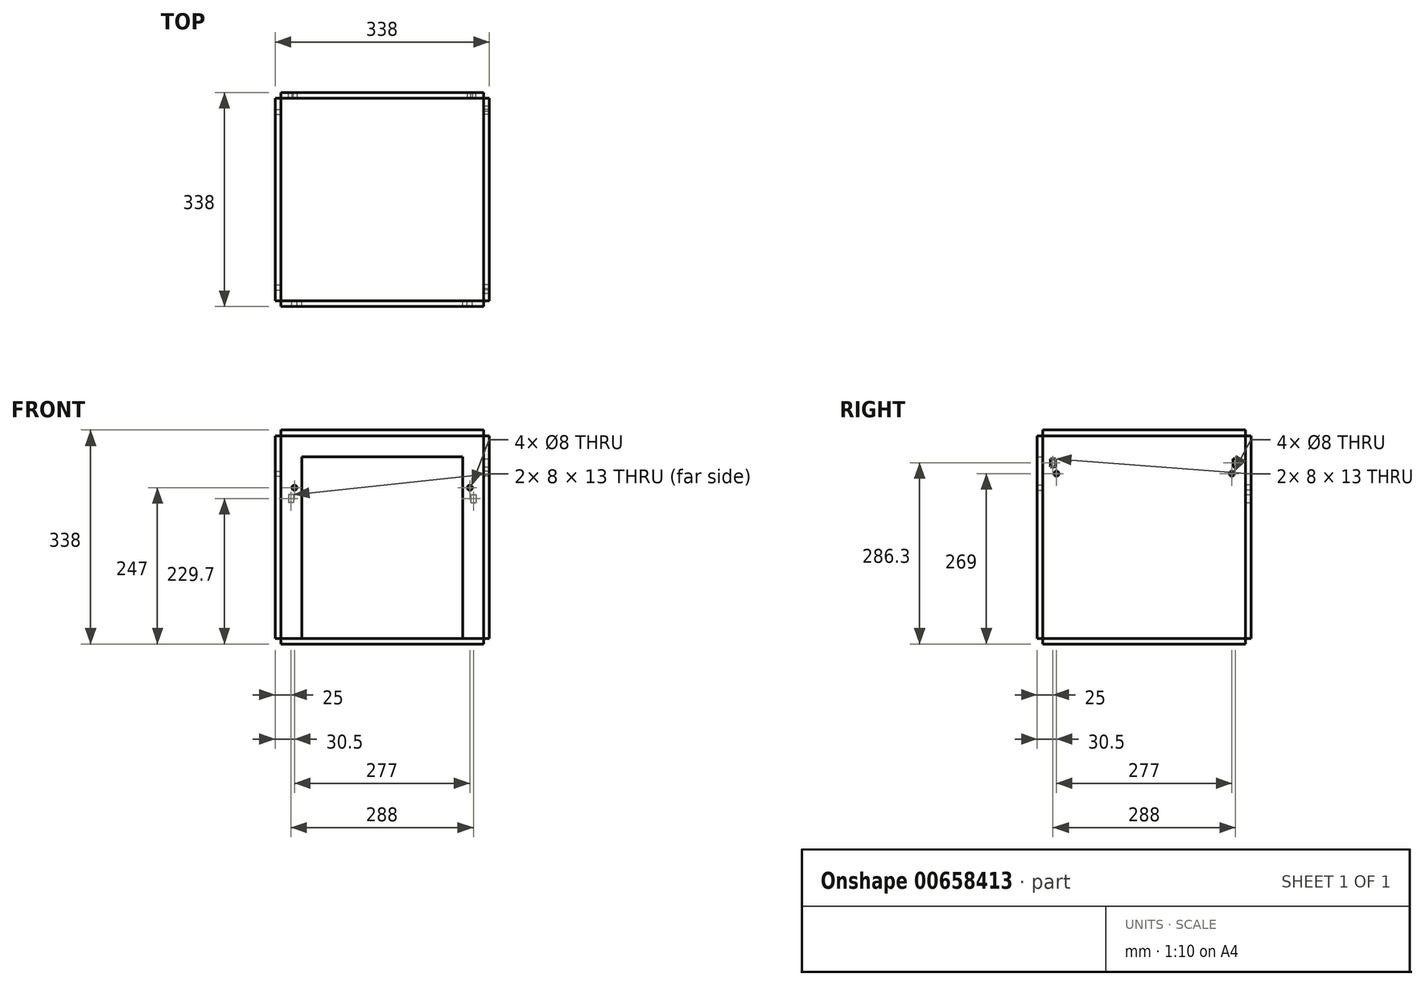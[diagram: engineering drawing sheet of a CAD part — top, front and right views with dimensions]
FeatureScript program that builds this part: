
annotation { "Feature Type Name" : "Feature", "Feature Type Description" : "" }
export const myFeature = defineFeature(function(context is Context, id is Id, definition is map)
    precondition{}
    {
        {
            assignVariable(context, id + "F0", {"name" : "wood", "anyValue" : 9});
        }
        {
            var Q0;
            Q0=qCreatedBy(makeId("Top.planeOp"),FACE);
            var sketch = newSketch(context, id + "F1", { "sketchPlane" : qUnion([Q0])});
            skLineSegment(sketch, "E0.bottom", {"start": v(160, 160) * mm, "end": v(-160, 160) * mm});
            skLineSegment(sketch, "E0.top", {"start": v(160, -160) * mm, "end": v(-160, -160) * mm});
            skLineSegment(sketch, "E0.left", {"start": v(160, 160) * mm, "end": v(160, -160) * mm});
            skLineSegment(sketch, "E0.right", {"start": v(-160, 160) * mm, "end": v(-160, -160) * mm});
            skPoint(sketch, "E0.middle", {"position": v(0, 0) * mm});
            skSolve(sketch);
        }
        {
            var Q0;
            Q0=makeQuery(id+"F1.imprint","IMPRINT",FACE,{"disambiguationData":[TD([[makeQuery(id+"F1.imprint","IMPRINT",EDGE,{"derivedFrom":sQuery(id+"F1.wireOp",EDGE,"E0.bottom")}),1.0]])]});
            extrude(context, id + "F2", {"entities" : qUnion([Q0]), "oppositeDirection" : true, "depth" : (getVariable(context, 'wood')) * mm, "offsetDistance" : 25 * mm});
        }
        {
            var Q0;
            Q0=makeQuery(id+"F2.opExtrude","SWEPT_FACE",FACE,{"disambiguationData":[OSD([sQuery(id+"F1.wireOp",EDGE,"E0.right")])]});
            var sketch = newSketch(context, id + "F3", { "sketchPlane" : qUnion([Q0])});
            skLineSegment(sketch, "E1.bottom", {"start": v(-160, 0) * mm, "end": v(160, 0) * mm});
            skLineSegment(sketch, "E1.top", {"start": v(-160, 320) * mm, "end": v(160, 320) * mm});
            skLineSegment(sketch, "E1.left", {"start": v(-160, 0) * mm, "end": v(-160, 320) * mm});
            skLineSegment(sketch, "E1.right", {"start": v(160, 0) * mm, "end": v(160, 320) * mm});
            skCircle(sketch, "E2", {"center": v(-138.5, 260) * mm, "radius": 4 * mm});
            skCircle(sketch, "E3.MirrorC", {"center": v(138.5, 260) * mm, "radius": 4 * mm});
            skSolve(sketch);
        }
        {
            var Q0;
            Q0=makeQuery(id+"F3.imprint","IMPRINT",FACE,{"disambiguationData":[TD([[makeQuery(id+"F3.imprint","IMPRINT",EDGE,{"derivedFrom":sQuery(id+"F3.wireOp",EDGE,"E1.bottom")}),1.0]])]});
            extrude(context, id + "F4", {"entities" : qUnion([Q0]), "depth" : (getVariable(context, 'wood')) * mm, "offsetDistance" : 25 * mm});
        }
        {
            var Q0;
            Q0=makeQuery(id+"F4.opExtrude","SWEPT_BODY",BODY,{"disambiguationData":[OSD([sQuery(id+"F3.wireOp",EDGE,"E1.bottom"),sQuery(id+"F3.wireOp",EDGE,"E1.top"),sQuery(id+"F3.wireOp",EDGE,"E1.left"),sQuery(id+"F3.wireOp",EDGE,"E1.right")])]});
            var Q1;
            Q1=qCreatedBy(makeId("Right.planeOp"),FACE);
            mirror(context, id + "F5", {"entities" : qUnion([Q0]), "mirrorPlane" : qUnion([Q1])});
        }
        {
            var Q0;
            Q0=makeQuery(id+"F2.opExtrude","SWEPT_FACE",FACE,{"disambiguationData":[OSD([sQuery(id+"F1.wireOp",EDGE,"E0.top")])]});
            var sketch = newSketch(context, id + "F6", { "sketchPlane" : qUnion([Q0])});
            skLineSegment(sketch, "E4.bottom", {"start": v(-160, 0) * mm, "end": v(160, 0) * mm});
            skLineSegment(sketch, "E4.top", {"start": v(-160, 320) * mm, "end": v(160, 320) * mm});
            skLineSegment(sketch, "E4.left", {"start": v(-160, 0) * mm, "end": v(-160, 320) * mm});
            skLineSegment(sketch, "E4.right", {"start": v(160, 0) * mm, "end": v(160, 320) * mm});
            skLineSegment(sketch, "E5", {"start": v(-127, 0) * mm, "end": v(-127, 287) * mm});
            skLineSegment(sketch, "E6.MirrorCS", {"start": v(127, 0) * mm, "end": v(127, 287) * mm});
            skLineSegment(sketch, "E7", {"start": v(-127, 287) * mm, "end": v(127, 287) * mm});
            skCircle(sketch, "E8", {"center": v(-138.5, 238) * mm, "radius": 4 * mm});
            skCircle(sketch, "E9.MirrorC", {"center": v(138.5, 238) * mm, "radius": 4 * mm});
            skSolve(sketch);
        }
        {
            var Q0;
            Q0=makeQuery(id+"F2.opExtrude","SWEPT_FACE",FACE,{"disambiguationData":[OSD([sQuery(id+"F1.wireOp",EDGE,"E0.bottom")])]});
            var sketch = newSketch(context, id + "F7", { "sketchPlane" : qUnion([Q0])});
            skLineSegment(sketch, "E10.bottom", {"start": v(-160, 0) * mm, "end": v(160, 0) * mm});
            skLineSegment(sketch, "E10.top", {"start": v(-160, 320) * mm, "end": v(160, 320) * mm});
            skLineSegment(sketch, "E10.left", {"start": v(-160, 0) * mm, "end": v(-160, 320) * mm});
            skLineSegment(sketch, "E10.right", {"start": v(160, 0) * mm, "end": v(160, 320) * mm});
            skCircle(sketch, "E11", {"center": v(-138.5, 238) * mm, "radius": 4 * mm});
            skCircle(sketch, "E12", {"center": v(138.5, 238) * mm, "radius": 4 * mm});
            skSolve(sketch);
        }
        {
            var Q0;
            Q0=makeQuery(id+"F7.imprint","IMPRINT",FACE,{"disambiguationData":[TD([[makeQuery(id+"F7.imprint","IMPRINT",EDGE,{"derivedFrom":sQuery(id+"F7.wireOp",EDGE,"E10.bottom")}),1.0]])]});
            extrude(context, id + "F8", {"entities" : qUnion([Q0]), "depth" : (getVariable(context, 'wood')) * mm, "offsetDistance" : 25 * mm});
        }
        {
            var Q0;
            Q0=makeQuery(id+"F6.imprint","IMPRINT",FACE,{"disambiguationData":[TD([[makeQuery(id+"F6.imprint","IMPRINT",EDGE,{"derivedFrom":sQuery(id+"F6.wireOp",EDGE,"E4.bottom")}),-1.0]])]});
            extrude(context, id + "F9", {"entities" : qUnion([Q0]), "depth" : (getVariable(context, 'wood')) * mm, "offsetDistance" : 25 * mm});
        }
        {
            var Q0;
            Q0=makeQuery(id+"F8.opExtrude","SWEPT_FACE",FACE,{"disambiguationData":[OSD([sQuery(id+"F7.wireOp",EDGE,"E10.top")])]});
            var sketch = newSketch(context, id + "F10", { "sketchPlane" : qUnion([Q0])});
            skLineSegment(sketch, "E13.bottom", {"start": v(-160, 160) * mm, "end": v(160, 160) * mm});
            skLineSegment(sketch, "E13.top", {"start": v(-160, -160) * mm, "end": v(160, -160) * mm});
            skLineSegment(sketch, "E13.left", {"start": v(-160, 160) * mm, "end": v(-160, -160) * mm});
            skLineSegment(sketch, "E13.right", {"start": v(160, 160) * mm, "end": v(160, -160) * mm});
            skSolve(sketch);
        }
        {
            var Q0;
            Q0=makeQuery(id+"F10.imprint","IMPRINT",FACE,{"disambiguationData":[TD([[makeQuery(id+"F10.imprint","IMPRINT",EDGE,{"derivedFrom":sQuery(id+"F10.wireOp",EDGE,"E13.bottom")}),1.0]])]});
            extrude(context, id + "F11", {"entities" : qUnion([Q0]), "depth" : (getVariable(context, 'wood')) * mm, "offsetDistance" : 25 * mm});
        }
        {
            var Q0;
            Q0=makeQuery(id+"F5.opPattern","COPY",FACE,{"derivedFrom":makeQuery(id+"F4.opExtrude","CAP_FACE",FACE,{"disambiguationData":[OSD([sQuery(id+"F3.wireOp",EDGE,"E1.bottom"),sQuery(id+"F3.wireOp",EDGE,"E1.top"),sQuery(id+"F3.wireOp",EDGE,"E1.left"),sQuery(id+"F3.wireOp",EDGE,"E1.right"),sQuery(id+"F3.wireOp",EDGE,"E2"),sQuery(id+"F3.wireOp",EDGE,"E3.MirrorC")])],"isStart":false}),"instanceName":"1"});
            var sketch = newSketch(context, id + "F12", { "sketchPlane" : qUnion([Q0])});
            skLineSegment(sketch, "E14.bottom", {"start": v(-140, 283.8) * mm, "end": v(-148, 283.8) * mm});
            skLineSegment(sketch, "E14.top", {"start": v(-140, 270.8) * mm, "end": v(-148, 270.8) * mm});
            skLineSegment(sketch, "E14.left", {"start": v(-140, 283.8) * mm, "end": v(-140, 270.8) * mm});
            skLineSegment(sketch, "E14.right", {"start": v(-148, 283.8) * mm, "end": v(-148, 270.8) * mm});
            skPoint(sketch, "E14.middle", {"position": v(-144, 277.3) * mm});
            skPoint(sketch, "E15", {"position": v(-138.5, 260) * mm});
            skLineSegment(sketch, "E16.MirrorCS", {"start": v(148, 283.8) * mm, "end": v(148, 270.8) * mm});
            skPoint(sketch, "E17.MirrorP", {"position": v(144, 277.3) * mm});
            skLineSegment(sketch, "E18.MirrorCS", {"start": v(140, 283.8) * mm, "end": v(148, 283.8) * mm});
            skLineSegment(sketch, "E19.MirrorCS", {"start": v(140, 283.8) * mm, "end": v(140, 270.8) * mm});
            skLineSegment(sketch, "E20.MirrorCS", {"start": v(140, 270.8) * mm, "end": v(148, 270.8) * mm});
            skSolve(sketch);
        }
        {
            var Q0;
            Q0=makeQuery(id+"F12.imprint","IMPRINT",FACE,{"disambiguationData":[TD([[makeQuery(id+"F12.imprint","IMPRINT",EDGE,{"derivedFrom":sQuery(id+"F12.wireOp",EDGE,"E14.bottom")}),1.0]])]});
            var Q1;
            Q1=makeQuery(id+"F12.imprint","IMPRINT",FACE,{"disambiguationData":[TD([[makeQuery(id+"F12.imprint","IMPRINT",EDGE,{"derivedFrom":sQuery(id+"F12.wireOp",EDGE,"E16.MirrorCS")}),-1.0]])]});
            extrude(context, id + "F13", {"entities" : qUnion([Q0, Q1]), "operationType" : NewBodyOperationType.REMOVE, "endBound" : BoundingType.UP_TO_NEXT, "oppositeDirection" : true, "depth" : 25 * mm, "offsetDistance" : 25 * mm});
        }
        {
            var Q0;
            Q0=makeQuery(id+"F8.opExtrude","CAP_FACE",FACE,{"disambiguationData":[OSD([sQuery(id+"F7.wireOp",EDGE,"E10.bottom"),sQuery(id+"F7.wireOp",EDGE,"E10.top"),sQuery(id+"F7.wireOp",EDGE,"E10.left"),sQuery(id+"F7.wireOp",EDGE,"E10.right"),sQuery(id+"F7.wireOp",EDGE,"E11"),sQuery(id+"F7.wireOp",EDGE,"E12")])],"isStart":false});
            var sketch = newSketch(context, id + "F14", { "sketchPlane" : qUnion([Q0])});
            skLineSegment(sketch, "E21.bottom", {"start": v(-140, 227.2) * mm, "end": v(-148, 227.2) * mm});
            skLineSegment(sketch, "E21.top", {"start": v(-140, 214.2) * mm, "end": v(-148, 214.2) * mm});
            skLineSegment(sketch, "E21.left", {"start": v(-140, 227.2) * mm, "end": v(-140, 214.2) * mm});
            skLineSegment(sketch, "E21.right", {"start": v(-148, 227.2) * mm, "end": v(-148, 214.2) * mm});
            skPoint(sketch, "E21.middle", {"position": v(-144, 220.7) * mm});
            skPoint(sketch, "E22", {"position": v(-138.5, 238) * mm});
            skPoint(sketch, "E23.MirrorP", {"position": v(144, 220.7) * mm});
            skLineSegment(sketch, "E24.MirrorCS", {"start": v(140, 227.2) * mm, "end": v(148, 227.2) * mm});
            skLineSegment(sketch, "E25.MirrorCS", {"start": v(140, 214.2) * mm, "end": v(148, 214.2) * mm});
            skLineSegment(sketch, "E26.MirrorCS", {"start": v(140, 227.2) * mm, "end": v(140, 214.2) * mm});
            skLineSegment(sketch, "E27.MirrorCS", {"start": v(148, 227.2) * mm, "end": v(148, 214.2) * mm});
            skSolve(sketch);
        }
        {
            var Q0;
            Q0=makeQuery(id+"F14.imprint","IMPRINT",FACE,{"disambiguationData":[TD([[makeQuery(id+"F14.imprint","IMPRINT",EDGE,{"derivedFrom":sQuery(id+"F14.wireOp",EDGE,"E21.bottom")}),1.0]])]});
            var Q1;
            Q1=makeQuery(id+"F14.imprint","IMPRINT",FACE,{"disambiguationData":[TD([[makeQuery(id+"F14.imprint","IMPRINT",EDGE,{"derivedFrom":sQuery(id+"F14.wireOp",EDGE,"E24.MirrorCS")}),-1.0]])]});
            extrude(context, id + "F15", {"entities" : qUnion([Q0, Q1]), "operationType" : NewBodyOperationType.REMOVE, "endBound" : BoundingType.UP_TO_NEXT, "oppositeDirection" : true, "depth" : 25 * mm, "offsetDistance" : 25 * mm});
        }
    });
